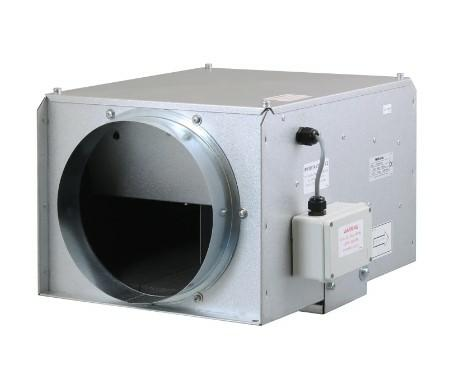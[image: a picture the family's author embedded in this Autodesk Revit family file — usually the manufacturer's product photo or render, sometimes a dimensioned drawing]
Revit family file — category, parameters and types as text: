
# Revit family: CADS_Vent-Axia_MechEquip_Fan_ACQ - SUPPLY
name_source: partatom
category: Mechanical Equipment
units: mm (PartAtom-declared; Revit-internal decimal feet)

## family parameters
Classification = None
Cut with Voids When Loaded = No
Host = Face
OmniClass Number = 23.75.35.17.11
OmniClass Title = Fans for Air Ductwork
Part Type = Normal
Room Calculation Point = No
Round Connector Dimension = Use Diameter
Shared = No

## types (10) — shared parameters
AirflowRateRange = 0.0 L/s
AssemblyPlace = UNKNOWN
AssetType = FIXED
Default Elevation = 1219 mm
DurationUnit = Year
ExteriorInsulation = No
Fitting Type = Ignore
GrossWeight = 0.00 kg
HasProtectiveEarth = No
IsExtendedWarranty = No
ManufacturerAddress = Fleming Way
Crawley 
RH10 9YX
Quantity = 1
RatedCurrent = 0 A
RatedVoltage = 0 V
Status = New
Type Image = CADS_Vent-Axia_MechEquip_Fan_ACQ.jpg
WorkingPressure = 0.0 Pa
zero-valued in all types: CADS_Index, CADS_Usage, ExpectedServiceLife, H, NumberOfPoles, OverallLength, SpigotLength, W

## per-type parameters (varying)
| type | EBHoffset | EBVoffset | L | ModelReference | NominalDiameter | NominalHeight | NominalLength | NominalWidth | OutOffset | Size | SpigotCLHeight |
| ACQ10012D | 110 mm  [stored 0.360892 ft] | 55 mm  [stored 0.180446 ft] | 360 mm | ACOUSTIC BOX FAN, 100 DIA SPIGOTS | 100 mm  [stored 0.328084 ft] | 190 mm | 400 mm | 310 mm  [stored 1.01706 ft] | 62 mm | 400mm x310mm x190mm | 94 mm |
| ACQ12512D | 109 mm | 49 mm | 360 mm | ACOUSTIC BOX FAN, 125 DIA SPIGOTS | 125 mm  [stored 0.410105 ft] | 190 mm | 400 mm | 310 mm  [stored 1.01706 ft] | 63 mm | 400mm x310mm x190mm | 94 mm |
| ACQ15012D | 92 mm | 94 mm | 360 mm | ACOUSTIC BOX FAN, 150 DIA SPIGOTS | 150 mm | 190 mm | 400 mm | 310 mm  [stored 1.01706 ft] | 50 mm | 400mm x310mm x190mm | 94 mm |
| ACQ16012D | 109 mm | 49 mm | 360 mm | ACOUSTIC BOX FAN, 160 DIA SPIGOTS | 160 mm  [stored 0.524934 ft] | 190 mm | 400 mm | 310 mm  [stored 1.01706 ft] | 45 mm  [stored 0.147638 ft] | 400mm x310mm x190mm | 94 mm |
| ACQ20012D | 93 mm | 92 mm | 415 mm | ACOUSTIC BOX FAN, 200 DIA SPIGOTS | 200 mm  [stored 0.656168 ft] | 285 mm  [stored 0.935039 ft] | 455 mm | 364 mm  [stored 1.19423 ft] | 55 mm  [stored 0.180446 ft] | 455mm x364mm x285mm | 140 mm |
| ACQ25012D | 92 mm | 92 mm | 415 mm | ACOUSTIC BOX FAN, 250 DIA SPIGOTS | 250 mm  [stored 0.82021 ft] | 285 mm  [stored 0.935039 ft] | 455 mm | 364 mm  [stored 1.19423 ft] | 30 mm  [stored 0.0984252 ft] | 455mm x364mm x285mm | 141 mm |
| ACQ31512LD | 90 mm | 123 mm | 415 mm | ACOUSTIC BOX FAN, 315 DIA SPIGOTS | 315 mm  [stored 1.03346 ft] | 348 mm  [stored 1.14173 ft] | 455 mm | 404 mm | 20 mm  [stored 0.0656168 ft] | 455mm x404mm x348mm | 173 mm |
| ACQ31514HD | 106 mm | 257 mm | 690 mm | ACOUSTIC BOX FAN, 315 DIA SPIGOTS | 315 mm  [stored 1.03346 ft] | 456 mm | 730 mm | 572 mm | 43 mm | 730mm x572mm x456mm | 227 mm |
| ACQ40014D | 106 mm | 257 mm | 690 mm | ACOUSTIC BOX FAN, 400 DIA SPIGOTS | 400 mm | 456 mm | 730 mm | 572 mm | 45 mm  [stored 0.147638 ft] | 730mm x572mm x456mm | 226 mm |
| ACQ50014D | 240 mm  [stored 0.787402 ft] | 392 mm | 878 mm | ACOUSTIC BOX FAN, 500 DIA SPIGOTS | 500 mm | 575 mm | 918 mm | 769 mm | 60 mm | 918mm x769mm x575mm | 286 mm |

note: column(s) folded — value = type name in every type: ModelNumber

note: [stored X ft] marks values corroborated as IEEE doubles in the binary element streams (Revit-internal decimal feet)

## geometry (parser evidence)
native form markers: Sweep x4
no freeform markers — native parametric forms only
